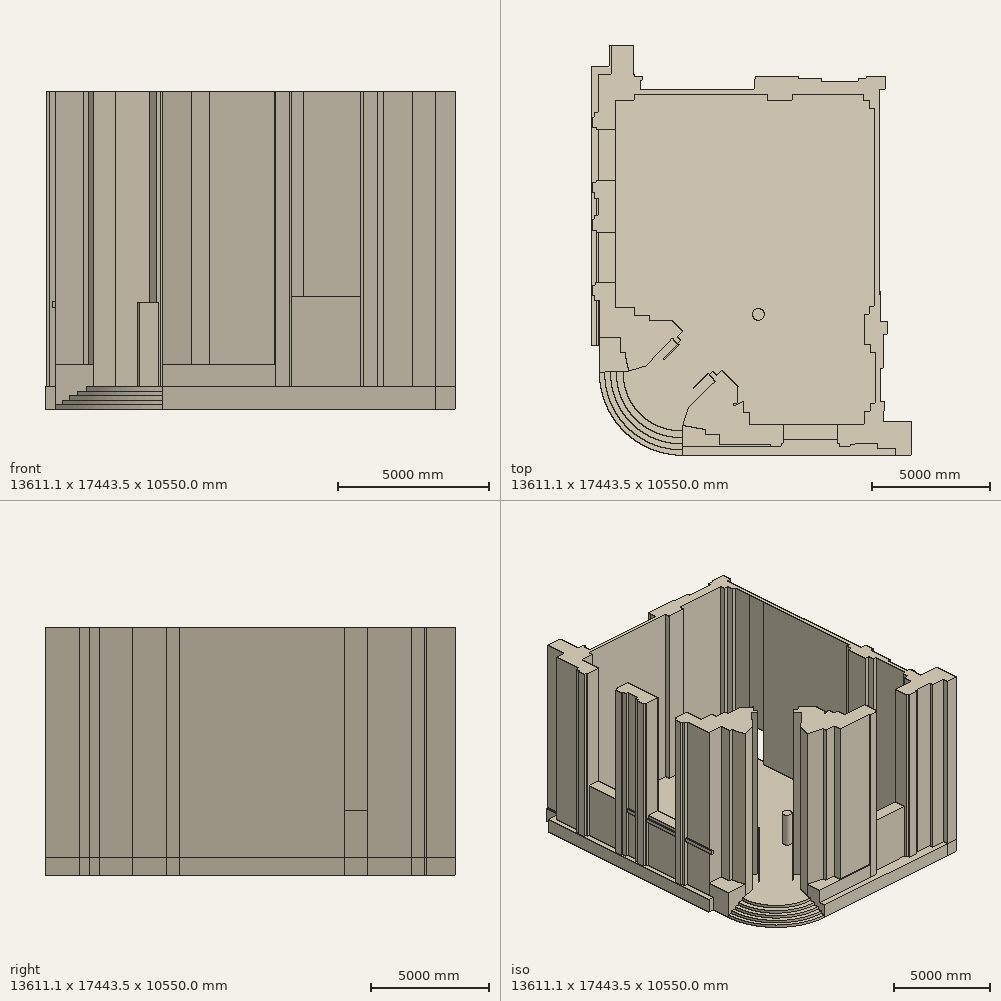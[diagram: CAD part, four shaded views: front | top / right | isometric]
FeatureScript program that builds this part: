
annotation { "Feature Type Name" : "Feature", "Feature Type Description" : "" }
export const myFeature = defineFeature(function(context is Context, id is Id, definition is map)
    precondition{}
    {
        {
            var Q0;
            Q0=qCreatedBy(makeId("Top.planeOp"),FACE);
            var sketch = newSketch(context, id + "F0", { "sketchPlane" : qUnion([Q0])});
            skLineSegment(sketch, "E0", {"start": v(0, 12125) * mm, "end": v(0, 8975) * mm});
            skLineSegment(sketch, "E1", {"start": v(0, 8975) * mm, "end": v(0, 0) * mm});
            skLineSegment(sketch, "E2", {"start": v(0, 0) * mm, "end": v(0, -1070) * mm});
            skLineSegment(sketch, "E3", {"start": v(7940.04, 3339.25) * mm, "end": v(6987.72, 3339.25) * mm});
            skLineSegment(sketch, "E4", {"start": v(6987.72, 3339.25) * mm, "end": v(6987.72, 3558.54) * mm});
            skLineSegment(sketch, "E5", {"start": v(6987.72, 3558.54) * mm, "end": v(6329.76, 3558.54) * mm});
            skLineSegment(sketch, "E6", {"start": v(6329.76, 3558.54) * mm, "end": v(6329.76, 3909.26) * mm});
            skLineSegment(sketch, "E7", {"start": v(6329.76, 3909.26) * mm, "end": v(5538.13, 3909.26) * mm});
            skLineSegment(sketch, "E8", {"start": v(5538.13, 3909.26) * mm, "end": v(5538.13, 4971.17) * mm});
            skLineSegment(sketch, "E9", {"start": v(5538.13, 4971.17) * mm, "end": v(4676.36, 4971.17) * mm});
            skLineSegment(sketch, "E10", {"start": v(4676.36, 4971.17) * mm, "end": v(4676.36, 4850.9) * mm});
            skLineSegment(sketch, "E11", {"start": v(4676.36, 4850.9) * mm, "end": v(4546.1, 4850.9) * mm});
            skLineSegment(sketch, "E12", {"start": v(4546.1, 4850.9) * mm, "end": v(4546.1, 4420.04) * mm});
            skLineSegment(sketch, "E13", {"start": v(4546.1, 4420.04) * mm, "end": v(4676.36, 4420.04) * mm});
            skLineSegment(sketch, "E14", {"start": v(4644.86, 4420.16) * mm, "end": v(4644.86, 4229.77) * mm});
            skLineSegment(sketch, "E15", {"start": v(4644.86, 4229.77) * mm, "end": v(4835.25, 4229.77) * mm});
            skLineSegment(sketch, "E16", {"start": v(4835.25, 4229.77) * mm, "end": v(4835.25, 2626.48) * mm});
            skLineSegment(sketch, "E17", {"start": v(4835.25, 2626.48) * mm, "end": v(5757.14, 2626.48) * mm});
            skLineSegment(sketch, "E18", {"start": v(5757.14, 2626.48) * mm, "end": v(5757.14, 2012.3) * mm});
            skLineSegment(sketch, "E19", {"start": v(5757.14, 2012.3) * mm, "end": v(5947.5, 2012.3) * mm});
            skLineSegment(sketch, "E20", {"start": v(5947.5, 2012.3) * mm, "end": v(6110.95, 1206.17) * mm, "construction": true});
            skLineSegment(sketch, "E21", {"start": v(6110.95, 1206.17) * mm, "end": v(6839.37, 1424) * mm});
            skLineSegment(sketch, "E22", {"start": v(6839.37, 1424) * mm, "end": v(7948.81, 2597.55) * mm});
            skLineSegment(sketch, "E23", {"start": v(7948.81, 2597.55) * mm, "end": v(8010.46, 2533.1) * mm});
            skLineSegment(sketch, "E24", {"start": v(8010.46, 2533.1) * mm, "end": v(8390.4, 2896.52) * mm});
            skLineSegment(sketch, "E25", {"start": v(8390.4, 2896.52) * mm, "end": v(7940.04, 3339.25) * mm});
            skArc(sketch, "E26", {"start": v(5947.5, 2012.3) * mm, "mid": v(5992.6, 1601.8) * mm, "end": v(6110.95, 1206.17) * mm});
            skLineSegment(sketch, "E27", {"start": v(5538.13, 4971.17) * mm, "end": v(5538.13, 7103.34) * mm});
            skLineSegment(sketch, "E28", {"start": v(5538.13, 7103.34) * mm, "end": v(4804.33, 7103.34) * mm});
            skLineSegment(sketch, "E29", {"start": v(4804.33, 7103.34) * mm, "end": v(4804.33, 4971.17) * mm});
            skLineSegment(sketch, "E30", {"start": v(5016.9, 7103.34) * mm, "end": v(5016.9, 4971.17) * mm});
            skLineSegment(sketch, "E31", {"start": v(5171.23, 7103.34) * mm, "end": v(5171.23, 4971.17) * mm});
            skLineSegment(sketch, "E32", {"start": v(5538.13, 7103.34) * mm, "end": v(5538.13, 9326.24) * mm});
            skLineSegment(sketch, "E33", {"start": v(5538.13, 9326.24) * mm, "end": v(4706.43, 9326.24) * mm});
            skLineSegment(sketch, "E34", {"start": v(4706.43, 9326.24) * mm, "end": v(4706.43, 9225.94) * mm});
            skLineSegment(sketch, "E35", {"start": v(4706.43, 9225.94) * mm, "end": v(4546.1, 9225.94) * mm});
            skLineSegment(sketch, "E36", {"start": v(4546.1, 9225.94) * mm, "end": v(4546.1, 8795.12) * mm});
            skLineSegment(sketch, "E37", {"start": v(4546.1, 8795.12) * mm, "end": v(4640.99, 8795.12) * mm});
            skLineSegment(sketch, "E38", {"start": v(4640.99, 8795.12) * mm, "end": v(4640.99, 8570.76) * mm});
            skLineSegment(sketch, "E39", {"start": v(4640.99, 8570.76) * mm, "end": v(4814.59, 8570.76) * mm});
            skLineSegment(sketch, "E40", {"start": v(4814.59, 8570.76) * mm, "end": v(4814.59, 7846.25) * mm});
            skLineSegment(sketch, "E41", {"start": v(4814.59, 7846.25) * mm, "end": v(4639.16, 7846.25) * mm});
            skLineSegment(sketch, "E42", {"start": v(4639.16, 7846.25) * mm, "end": v(4639.16, 7645.84) * mm});
            skLineSegment(sketch, "E43", {"start": v(4639.16, 7645.84) * mm, "end": v(4546.1, 7645.84) * mm});
            skLineSegment(sketch, "E44", {"start": v(4546.1, 7645.84) * mm, "end": v(4546.1, 7191.3) * mm});
            skLineSegment(sketch, "E45", {"start": v(4546.1, 7191.3) * mm, "end": v(4706.43, 7191.3) * mm});
            skLineSegment(sketch, "E46", {"start": v(4706.43, 7191.3) * mm, "end": v(4706.43, 7103.34) * mm});
            skLineSegment(sketch, "E47", {"start": v(4706.43, 7103.34) * mm, "end": v(4804.33, 7103.34) * mm});
            skLineSegment(sketch, "E48", {"start": v(5538.13, 9326.24) * mm, "end": v(5538.13, 11477.09) * mm});
            skLineSegment(sketch, "E49", {"start": v(5538.13, 11477.09) * mm, "end": v(4706.43, 11477.09) * mm});
            skLineSegment(sketch, "E50", {"start": v(5195.88, 11477.09) * mm, "end": v(5195.88, 9326.24) * mm});
            skLineSegment(sketch, "E51", {"start": v(5023.03, 11477.09) * mm, "end": v(5023.03, 9326.24) * mm});
            skLineSegment(sketch, "E52", {"start": v(4822.61, 11477.09) * mm, "end": v(4822.61, 9326.24) * mm});
            skLineSegment(sketch, "E53", {"start": v(5538.13, 11477.09) * mm, "end": v(5538.13, 12718.59) * mm});
            skLineSegment(sketch, "E54", {"start": v(5538.13, 12718.59) * mm, "end": v(6328.59, 12718.59) * mm});
            skLineSegment(sketch, "E55", {"start": v(6328.59, 12718.59) * mm, "end": v(6328.59, 12979.12) * mm});
            skLineSegment(sketch, "E56", {"start": v(6328.59, 12979.12) * mm, "end": v(6579.1, 12979.12) * mm});
            skLineSegment(sketch, "E57", {"start": v(6579.1, 12979.12) * mm, "end": v(6579.1, 13590.38) * mm});
            skLineSegment(sketch, "E58", {"start": v(6579.1, 13590.38) * mm, "end": v(6679.3, 13590.38) * mm});
            skLineSegment(sketch, "E59", {"start": v(6679.3, 13590.38) * mm, "end": v(6679.3, 13743.22) * mm});
            skLineSegment(sketch, "E60", {"start": v(6679.3, 13743.22) * mm, "end": v(6323.82, 13743.22) * mm});
            skLineSegment(sketch, "E61", {"start": v(6323.82, 13743.22) * mm, "end": v(6323.82, 13838.41) * mm});
            skLineSegment(sketch, "E62", {"start": v(6323.82, 13838.41) * mm, "end": v(6296.26, 13838.41) * mm});
            skLineSegment(sketch, "E63", {"start": v(6296.26, 13838.41) * mm, "end": v(6296.26, 15059.07) * mm});
            skLineSegment(sketch, "E64", {"start": v(6296.26, 15059.07) * mm, "end": v(5357.4, 15059.07) * mm});
            skLineSegment(sketch, "E65", {"start": v(5357.4, 15059.07) * mm, "end": v(5357.4, 13838.41) * mm});
            skLineSegment(sketch, "E66", {"start": v(5357.4, 13838.41) * mm, "end": v(4806.28, 13838.41) * mm});
            skLineSegment(sketch, "E67", {"start": v(4806.28, 13838.41) * mm, "end": v(4806.28, 12207.37) * mm});
            skLineSegment(sketch, "E68", {"start": v(4806.28, 12207.37) * mm, "end": v(4616.24, 12207.37) * mm});
            skLineSegment(sketch, "E69", {"start": v(4616.24, 12207.37) * mm, "end": v(4616.24, 12006.96) * mm});
            skLineSegment(sketch, "E70", {"start": v(4616.24, 12006.96) * mm, "end": v(4546.1, 12006.96) * mm});
            skLineSegment(sketch, "E71", {"start": v(4546.1, 12006.96) * mm, "end": v(4546.1, 11556.04) * mm});
            skLineSegment(sketch, "E72", {"start": v(4546.1, 11556.04) * mm, "end": v(4706.43, 11556.04) * mm});
            skLineSegment(sketch, "E73", {"start": v(4706.43, 11556.04) * mm, "end": v(4706.43, 11477.09) * mm});
            skLineSegment(sketch, "E74", {"start": v(4546.1, 11556.04) * mm, "end": v(4546.1, 9225.94) * mm, "construction": true});
            skLineSegment(sketch, "E75", {"start": v(4546.1, 7191.3) * mm, "end": v(4546.1, 4850.9) * mm, "construction": true});
            skLineSegment(sketch, "E76", {"start": v(6579.1, 12979.12) * mm, "end": v(11443.66, 12979.12) * mm});
            skLineSegment(sketch, "E77", {"start": v(11443.66, 12979.12) * mm, "end": v(11443.66, 13185.96) * mm});
            skLineSegment(sketch, "E78", {"start": v(11443.66, 13185.96) * mm, "end": v(6579.1, 13185.96) * mm});
            skLineSegment(sketch, "E79", {"start": v(11443.66, 12979.12) * mm, "end": v(11992.54, 12979.12) * mm});
            skLineSegment(sketch, "E80", {"start": v(11992.54, 12979.12) * mm, "end": v(11992.54, 12727.02) * mm});
            skLineSegment(sketch, "E81", {"start": v(11992.54, 12727.02) * mm, "end": v(13064.75, 12727.02) * mm});
            skLineSegment(sketch, "E82", {"start": v(13064.75, 12727.02) * mm, "end": v(13064.75, 12979.12) * mm});
            skLineSegment(sketch, "E83", {"start": v(13064.75, 12979.12) * mm, "end": v(16070.92, 12979.12) * mm});
            skLineSegment(sketch, "E84", {"start": v(16070.92, 12979.12) * mm, "end": v(16070.92, 12727.02) * mm});
            skLineSegment(sketch, "E85", {"start": v(16070.92, 12727.02) * mm, "end": v(16321.44, 12727.02) * mm});
            skLineSegment(sketch, "E86", {"start": v(16321.44, 12727.02) * mm, "end": v(16321.44, 12366.28) * mm});
            skLineSegment(sketch, "E87", {"start": v(16321.44, 12366.28) * mm, "end": v(16531.87, 12366.28) * mm});
            skLineSegment(sketch, "E88", {"start": v(16531.87, 12366.28) * mm, "end": v(16531.87, 11314.12) * mm});
            skLineSegment(sketch, "E89", {"start": v(16531.87, 11314.12) * mm, "end": v(16752.32, 11314.12) * mm});
            skLineSegment(sketch, "E90", {"start": v(16752.32, 11314.12) * mm, "end": v(16752.32, 13185.96) * mm});
            skLineSegment(sketch, "E91", {"start": v(16752.32, 13185.96) * mm, "end": v(16992.82, 13185.96) * mm});
            skLineSegment(sketch, "E92", {"start": v(16992.82, 13185.96) * mm, "end": v(16992.82, 13739.1) * mm});
            skLineSegment(sketch, "E93", {"start": v(16992.82, 13739.1) * mm, "end": v(16201.19, 13739.1) * mm});
            skLineSegment(sketch, "E94", {"start": v(16201.19, 13739.1) * mm, "end": v(16201.19, 13658.94) * mm});
            skLineSegment(sketch, "E95", {"start": v(16201.19, 13658.94) * mm, "end": v(15860.49, 13658.94) * mm});
            skLineSegment(sketch, "E96", {"start": v(15860.49, 13658.94) * mm, "end": v(15860.49, 13508.63) * mm});
            skLineSegment(sketch, "E97", {"start": v(15860.49, 13508.63) * mm, "end": v(14287.26, 13508.63) * mm});
            skLineSegment(sketch, "E98", {"start": v(14287.26, 13508.63) * mm, "end": v(14287.26, 13658.94) * mm});
            skLineSegment(sketch, "E99", {"start": v(14287.26, 13658.94) * mm, "end": v(13295.22, 13658.94) * mm});
            skLineSegment(sketch, "E100", {"start": v(13295.22, 13658.94) * mm, "end": v(13295.22, 13739.1) * mm});
            skLineSegment(sketch, "E101", {"start": v(13295.22, 13739.1) * mm, "end": v(11495.49, 13739.1) * mm});
            skLineSegment(sketch, "E102", {"start": v(11495.49, 13739.1) * mm, "end": v(11443.66, 13556.66) * mm});
            skLineSegment(sketch, "E103", {"start": v(11443.66, 13556.66) * mm, "end": v(11443.66, 13185.96) * mm});
            skLineSegment(sketch, "E104", {"start": v(16749.46, 10318.63) * mm, "end": v(16529, 10318.63) * mm});
            skLineSegment(sketch, "E105", {"start": v(16529, 10318.63) * mm, "end": v(16529, 3949.74) * mm});
            skLineSegment(sketch, "E106", {"start": v(16529, 3949.74) * mm, "end": v(16348.32, 3949.74) * mm});
            skLineSegment(sketch, "E107", {"start": v(16348.32, 3949.74) * mm, "end": v(16348.32, 3602.54) * mm});
            skLineSegment(sketch, "E108", {"start": v(16348.32, 3602.54) * mm, "end": v(16107.41, 3602.54) * mm});
            skLineSegment(sketch, "E109", {"start": v(16107.41, 3602.54) * mm, "end": v(16107.41, 2348.35) * mm});
            skLineSegment(sketch, "E110", {"start": v(16107.41, 2348.35) * mm, "end": v(16371.6, 2348.35) * mm});
            skLineSegment(sketch, "E111", {"start": v(16371.6, 2348.35) * mm, "end": v(16371.6, 2000.51) * mm});
            skLineSegment(sketch, "E112", {"start": v(16371.6, 2000.51) * mm, "end": v(16571.77, 2000.51) * mm});
            skLineSegment(sketch, "E113", {"start": v(16571.77, 2000.51) * mm, "end": v(16571.77, -172.06) * mm});
            skLineSegment(sketch, "E114", {"start": v(16571.77, -172.06) * mm, "end": v(16387.34, -172.06) * mm});
            skLineSegment(sketch, "E115", {"start": v(16387.34, -172.06) * mm, "end": v(16387.34, -531.4) * mm});
            skLineSegment(sketch, "E116", {"start": v(16387.34, -531.4) * mm, "end": v(16107.41, -531.4) * mm});
            skLineSegment(sketch, "E117", {"start": v(16107.41, -531.4) * mm, "end": v(16107.41, -1052.2) * mm});
            skLineSegment(sketch, "E118", {"start": v(16107.41, -1052.2) * mm, "end": v(14950.76, -1052.2) * mm});
            skLineSegment(sketch, "E119", {"start": v(14950.76, -1052.2) * mm, "end": v(14950.76, -1860.02) * mm});
            skLineSegment(sketch, "E120", {"start": v(14950.76, -1860.02) * mm, "end": v(15058.18, -1860.02) * mm});
            skLineSegment(sketch, "E121", {"start": v(15058.18, -1860.02) * mm, "end": v(15058.18, -1999.96) * mm});
            skLineSegment(sketch, "E122", {"start": v(15058.18, -1999.96) * mm, "end": v(15524.06, -1999.96) * mm});
            skLineSegment(sketch, "E123", {"start": v(15524.06, -1999.96) * mm, "end": v(15524.06, -1918.48) * mm});
            skLineSegment(sketch, "E124", {"start": v(15524.06, -1918.48) * mm, "end": v(15724.23, -1918.48) * mm});
            skLineSegment(sketch, "E125", {"start": v(15724.23, -1918.48) * mm, "end": v(15724.23, -1883.05) * mm});
            skLineSegment(sketch, "E126", {"start": v(15724.23, -1883.05) * mm, "end": v(16678.15, -1883.05) * mm});
            skLineSegment(sketch, "E127", {"start": v(16678.15, -1883.05) * mm, "end": v(16678.15, -2084.88) * mm});
            skLineSegment(sketch, "E128", {"start": v(16678.15, -2084.88) * mm, "end": v(17458.3, -2084.88) * mm});
            skLineSegment(sketch, "E129", {"start": v(17458.3, -2084.88) * mm, "end": v(17458.3, -2384.45) * mm});
            skLineSegment(sketch, "E130", {"start": v(17458.3, -2384.45) * mm, "end": v(18116.83, -2384.45) * mm});
            skLineSegment(sketch, "E131", {"start": v(18116.83, -2384.45) * mm, "end": v(18116.83, -946.5) * mm});
            skLineSegment(sketch, "E132", {"start": v(18116.83, -946.5) * mm, "end": v(16924.38, -946.5) * mm});
            skLineSegment(sketch, "E133", {"start": v(16924.38, -946.5) * mm, "end": v(16924.38, -515.61) * mm});
            skLineSegment(sketch, "E134", {"start": v(16924.38, -515.61) * mm, "end": v(16984.5, -515.61) * mm});
            skLineSegment(sketch, "E135", {"start": v(16984.5, -515.61) * mm, "end": v(16984.5, -104.77) * mm});
            skLineSegment(sketch, "E136", {"start": v(16984.5, -104.77) * mm, "end": v(16784.1, -104.77) * mm});
            skLineSegment(sketch, "E137", {"start": v(16784.1, -104.77) * mm, "end": v(16784.1, 1320.73) * mm});
            skLineSegment(sketch, "E138", {"start": v(16784.1, 1320.73) * mm, "end": v(16914.18, 1320.73) * mm});
            skLineSegment(sketch, "E139", {"start": v(16914.18, 1320.73) * mm, "end": v(16914.18, 2753.98) * mm});
            skLineSegment(sketch, "E140", {"start": v(16914.18, 2753.98) * mm, "end": v(17110.48, 2753.98) * mm});
            skLineSegment(sketch, "E141", {"start": v(17110.48, 2753.98) * mm, "end": v(17110.48, 3310.12) * mm});
            skLineSegment(sketch, "E142", {"start": v(17110.48, 3310.12) * mm, "end": v(16784.1, 3310.12) * mm});
            skLineSegment(sketch, "E143", {"start": v(16784.1, 3310.12) * mm, "end": v(16749.46, 10318.63) * mm});
            skLineSegment(sketch, "E144", {"start": v(10955.86, -104.77) * mm, "end": v(10957.98, -534) * mm});
            skLineSegment(sketch, "E145", {"start": v(10957.98, -534) * mm, "end": v(11210.94, -534) * mm});
            skLineSegment(sketch, "E146", {"start": v(11210.94, -534) * mm, "end": v(11213.5, -1052.2) * mm});
            skLineSegment(sketch, "E147", {"start": v(11213.5, -1052.2) * mm, "end": v(12670.58, -1052.2) * mm});
            skLineSegment(sketch, "E148", {"start": v(12670.58, -1052.2) * mm, "end": v(12674.57, -1860.02) * mm});
            skLineSegment(sketch, "E149", {"start": v(12674.57, -1860.02) * mm, "end": v(12599.73, -1860.02) * mm});
            skLineSegment(sketch, "E150", {"start": v(12599.73, -1860.02) * mm, "end": v(12600.5, -2014.87) * mm});
            skLineSegment(sketch, "E151", {"start": v(12600.5, -2014.87) * mm, "end": v(12124.99, -2014.87) * mm});
            skLineSegment(sketch, "E152", {"start": v(12124.99, -2014.87) * mm, "end": v(12124.6, -1937.04) * mm});
            skLineSegment(sketch, "E153", {"start": v(12124.6, -1937.04) * mm, "end": v(9963.87, -1937.04) * mm});
            skLineSegment(sketch, "E154", {"start": v(9963.87, -1937.04) * mm, "end": v(9961.67, -1490.58) * mm});
            skLineSegment(sketch, "E155", {"start": v(9961.67, -1490.58) * mm, "end": v(9368.68, -1490.58) * mm});
            skLineSegment(sketch, "E156", {"start": v(9368.68, -1490.58) * mm, "end": v(9367.67, -1285.06) * mm});
            skLineSegment(sketch, "E157", {"start": v(9367.67, -1285.06) * mm, "end": v(8390.86, -1107.98) * mm});
            skLineSegment(sketch, "E158", {"start": v(8390.86, -1107.98) * mm, "end": v(8624.7, -378.16) * mm});
            skLineSegment(sketch, "E159", {"start": v(8624.7, -378.16) * mm, "end": v(9779.65, 762.62) * mm});
            skLineSegment(sketch, "E160", {"start": v(9779.65, 762.62) * mm, "end": v(9691.6, 851.76) * mm});
            skLineSegment(sketch, "E161", {"start": v(9691.6, 851.76) * mm, "end": v(10076.1, 1231.53) * mm});
            skLineSegment(sketch, "E162", {"start": v(10076.1, 1231.53) * mm, "end": v(10739.2, 560.18) * mm});
            skLineSegment(sketch, "E163", {"start": v(10739.2, 560.18) * mm, "end": v(10707.47, -183.95) * mm});
            skLineSegment(sketch, "E164", {"start": v(10707.47, -183.95) * mm, "end": v(10517.08, -183.95) * mm});
            skLineSegment(sketch, "E165", {"start": v(10517.08, -183.95) * mm, "end": v(10588.48, -271.63) * mm});
            skLineSegment(sketch, "E166", {"start": v(10588.48, -271.63) * mm, "end": v(10955.86, -104.77) * mm});
            skLineSegment(sketch, "E167", {"start": v(9691.6, 851.76) * mm, "end": v(9504.05, 1041.64) * mm});
            skPoint(sketch, "E167.endSnap0", {"position": v(9883.85, 1041.64) * mm});
            skLineSegment(sketch, "E168", {"start": v(9504.05, 1041.64) * mm, "end": v(9660, 1195.68) * mm});
            skLineSegment(sketch, "E169", {"start": v(9660, 1195.68) * mm, "end": v(9847.55, 1005.8) * mm});
            skLineSegment(sketch, "E170", {"start": v(9489.72, 1069.4) * mm, "end": v(8853.27, 440.76) * mm});
            skLineSegment(sketch, "E171", {"start": v(8853.27, 440.76) * mm, "end": v(8828.52, 465.82) * mm});
            skLineSegment(sketch, "E172", {"start": v(8828.52, 465.82) * mm, "end": v(9464.77, 1094.27) * mm});
            skLineSegment(sketch, "E173", {"start": v(9464.77, 1094.27) * mm, "end": v(9489.72, 1069.4) * mm});
            skLineSegment(sketch, "E174", {"start": v(8155.17, 2671.52) * mm, "end": v(8318.08, 2501.2) * mm});
            skLineSegment(sketch, "E175", {"start": v(8318.08, 2501.2) * mm, "end": v(8175.6, 2360.46) * mm});
            skLineSegment(sketch, "E176", {"start": v(8175.6, 2360.46) * mm, "end": v(8010.46, 2533.1) * mm});
            skLineSegment(sketch, "E177", {"start": v(8208.1, 2343.48) * mm, "end": v(7569.28, 1709.68) * mm});
            skLineSegment(sketch, "E178", {"start": v(7569.28, 1709.68) * mm, "end": v(7610.45, 1668.18) * mm});
            skLineSegment(sketch, "E179", {"start": v(7610.45, 1668.18) * mm, "end": v(8251.91, 2304.62) * mm});
            skLineSegment(sketch, "E180", {"start": v(8251.91, 2304.62) * mm, "end": v(8208.1, 2343.48) * mm});
            skLineSegment(sketch, "E181", {"start": v(14950.76, -1052.2) * mm, "end": v(12670.58, -1052.2) * mm});
            skLineSegment(sketch, "E182", {"start": v(12672.08, -1355.72) * mm, "end": v(14950.76, -1344.46) * mm});
            skLineSegment(sketch, "E183", {"start": v(14950.76, -1511.59) * mm, "end": v(12672.85, -1511.59) * mm});
            skLineSegment(sketch, "E184", {"start": v(12673.9, -1724.2) * mm, "end": v(14950.76, -1712.95) * mm});
            skArc(sketch, "E185", {"start": v(6839.37, 1424) * mm, "mid": v(7508.6, 301.59) * mm, "end": v(8624.7, -378.16) * mm});
            skLineSegment(sketch, "E186", {"start": v(4835.25, 2626.48) * mm, "end": v(4835.25, 1157.72) * mm});
            skLineSegment(sketch, "E187", {"start": v(4835.25, 1157.72) * mm, "end": v(6110.95, 1206.17) * mm});
            skLineSegment(sketch, "E188", {"start": v(8390.86, -1107.98) * mm, "end": v(8390.86, -2375.98) * mm});
            skLineSegment(sketch, "E189", {"start": v(8390.86, -2375.98) * mm, "end": v(17458.3, -2384.45) * mm});
            skArc(sketch, "E190", {"start": v(5855.53, 1196.47) * mm, "mid": v(6569.5, -622.26) * mm, "end": v(8390.86, -1329.48) * mm});
            skArc(sketch, "E191", {"start": v(5563.67, 1185.38) * mm, "mid": v(6369.39, -830.3) * mm, "end": v(8390.86, -1621.35) * mm});
            skArc(sketch, "E192", {"start": v(5314.58, 1175.92) * mm, "mid": v(6199.93, -1011.75) * mm, "end": v(8390.86, -1889) * mm});
            skArc(sketch, "E193", {"start": v(5065.76, 1166.47) * mm, "mid": v(6026.82, -1192.56) * mm, "end": v(8390.86, -2141.24) * mm});
            skArc(sketch, "E194", {"start": v(4835.25, 1157.72) * mm, "mid": v(5878, -1348.75) * mm, "end": v(8390.86, -2375.98) * mm});
            skLineSegment(sketch, "E195", {"start": v(16749.46, 10318.63) * mm, "end": v(16752.32, 11314.12) * mm});
            skLineSegment(sketch, "E196", {"start": v(16531.87, 11314.12) * mm, "end": v(16529, 10318.63) * mm});
            skLineSegment(sketch, "E197", {"start": v(12124.99, -2014.87) * mm, "end": v(8390.86, -2011.38) * mm});
            skLineSegment(sketch, "E198", {"start": v(4835.25, 2295.94) * mm, "end": v(4505.74, 2295.94) * mm});
            skLineSegment(sketch, "E199", {"start": v(4505.74, 2295.94) * mm, "end": v(4505.74, 14151.04) * mm});
            skLineSegment(sketch, "E200", {"start": v(4505.74, 14151.04) * mm, "end": v(5251.5, 14151.04) * mm});
            skLineSegment(sketch, "E201", {"start": v(5251.5, 14151.04) * mm, "end": v(5251.5, 15059.07) * mm});
            skLineSegment(sketch, "E202", {"start": v(5251.5, 15059.07) * mm, "end": v(5357.4, 15059.07) * mm});
            skSolve(sketch);
        }
        {
            var Q0;
            Q0=makeQuery(id+"F0.imprint","IMPRINT",FACE,{"disambiguationData":[TD([[makeQuery(id+"F0.imprint","IMPRINT",EDGE,{"derivedFrom":sQuery(id+"F0.wireOp",EDGE,"E3")}),1.0]])]});
            var Q1;
            {var subQ5=sQuery(id+"F0.wireOp",EDGE,"E32");Q1=makeQuery(id+"F0.imprint","IMPRINT",FACE,{"disambiguationData":[TD([[makeQuery(id+"F0.imprint","IMPRINT",EDGE,{"derivedFrom":subQ5}),1.0]])]});}
            var Q2;
            {var subQ8=sQuery(id+"F0.wireOp",EDGE,"E53");Q2=makeQuery(id+"F0.imprint","IMPRINT",FACE,{"disambiguationData":[TD([[makeQuery(id+"F0.imprint","IMPRINT",EDGE,{"derivedFrom":subQ8}),1.0]])]});}
            var Q3;
            {var subQ0=sQuery(id+"F0.wireOp",EDGE,"E76");Q3=makeQuery(id+"F0.imprint","IMPRINT",FACE,{"disambiguationData":[TD([[makeQuery(id+"F0.imprint","IMPRINT",EDGE,{"derivedFrom":subQ0}),1.0]])]});}
            var Q4;
            Q4=makeQuery(id+"F0.imprint","IMPRINT",FACE,{"disambiguationData":[TD([[makeQuery(id+"F0.imprint","IMPRINT",EDGE,{"derivedFrom":sQuery(id+"F0.wireOp",EDGE,"E77")}),-1.0]])]});
            var Q5;
            Q5=makeQuery(id+"F0.imprint","IMPRINT",FACE,{"disambiguationData":[TD([[makeQuery(id+"F0.imprint","IMPRINT",EDGE,{"derivedFrom":sQuery(id+"F0.wireOp",EDGE,"E104")}),1.0]])]});
            var Q6;
            Q6=makeQuery(id+"F0.imprint","IMPRINT",FACE,{"disambiguationData":[TD([[makeQuery(id+"F0.imprint","IMPRINT",EDGE,{"derivedFrom":sQuery(id+"F0.wireOp",EDGE,"E144")}),-1.0]])]});
            var Q7;
            {var subQ0=sQuery(id+"F0.wireOp",EDGE,"E167");Q7=makeQuery(id+"F0.imprint","IMPRINT",FACE,{"disambiguationData":[TD([[makeQuery(id+"F0.imprint","IMPRINT",EDGE,{"derivedFrom":subQ0}),-1.0]])]});}
            var Q8;
            {var subQ2=sQuery(id+"F0.wireOp",EDGE,"E174");Q8=makeQuery(id+"F0.imprint","IMPRINT",FACE,{"disambiguationData":[TD([[makeQuery(id+"F0.imprint","IMPRINT",EDGE,{"derivedFrom":subQ2}),-1.0]])]});}
            extrude(context, id + "F1", {"entities" : qUnion([Q0, Q1, Q2, Q3, Q4, Q5, Q6, Q7, Q8]), "depth" : 9800 * mm, "offsetDistance" : 25 * mm});
        }
        {
            var Q0;
            Q0=makeQuery(id+"F0.imprint","IMPRINT",FACE,{"disambiguationData":[TD([[makeQuery(id+"F0.imprint","IMPRINT",EDGE,{"derivedFrom":sQuery(id+"F0.wireOp",EDGE,"E89")}),-1.0]])]});
            var Q1;
            Q1=makeQuery(id+"F1.opExtrude","CAP_FACE",FACE,{"disambiguationData":[OSD([sQuery(id+"F0.wireOp",EDGE,"E49"),sQuery(id+"F0.wireOp",EDGE,"E53"),sQuery(id+"F0.wireOp",EDGE,"E54"),sQuery(id+"F0.wireOp",EDGE,"E55"),sQuery(id+"F0.wireOp",EDGE,"E56"),sQuery(id+"F0.wireOp",EDGE,"E57"),sQuery(id+"F0.wireOp",EDGE,"E58"),sQuery(id+"F0.wireOp",EDGE,"E59"),sQuery(id+"F0.wireOp",EDGE,"E60"),sQuery(id+"F0.wireOp",EDGE,"E61"),sQuery(id+"F0.wireOp",EDGE,"E62"),sQuery(id+"F0.wireOp",EDGE,"E63"),sQuery(id+"F0.wireOp",EDGE,"E64"),sQuery(id+"F0.wireOp",EDGE,"E65"),sQuery(id+"F0.wireOp",EDGE,"E66"),sQuery(id+"F0.wireOp",EDGE,"E67"),sQuery(id+"F0.wireOp",EDGE,"E68"),sQuery(id+"F0.wireOp",EDGE,"E69"),sQuery(id+"F0.wireOp",EDGE,"E70"),sQuery(id+"F0.wireOp",EDGE,"E71"),sQuery(id+"F0.wireOp",EDGE,"E72"),sQuery(id+"F0.wireOp",EDGE,"E73"),sQuery(id+"F0.wireOp",EDGE,"E76"),sQuery(id+"F0.wireOp",EDGE,"E78"),sQuery(id+"F0.wireOp",EDGE,"E79"),sQuery(id+"F0.wireOp",EDGE,"E80"),sQuery(id+"F0.wireOp",EDGE,"E81"),sQuery(id+"F0.wireOp",EDGE,"E82"),sQuery(id+"F0.wireOp",EDGE,"E83"),sQuery(id+"F0.wireOp",EDGE,"E84"),sQuery(id+"F0.wireOp",EDGE,"E85"),sQuery(id+"F0.wireOp",EDGE,"E86"),sQuery(id+"F0.wireOp",EDGE,"E87"),sQuery(id+"F0.wireOp",EDGE,"E88"),sQuery(id+"F0.wireOp",EDGE,"E89"),sQuery(id+"F0.wireOp",EDGE,"E90"),sQuery(id+"F0.wireOp",EDGE,"E91"),sQuery(id+"F0.wireOp",EDGE,"E92"),sQuery(id+"F0.wireOp",EDGE,"E93"),sQuery(id+"F0.wireOp",EDGE,"E94"),sQuery(id+"F0.wireOp",EDGE,"E95"),sQuery(id+"F0.wireOp",EDGE,"E96"),sQuery(id+"F0.wireOp",EDGE,"E97"),sQuery(id+"F0.wireOp",EDGE,"E98"),sQuery(id+"F0.wireOp",EDGE,"E99"),sQuery(id+"F0.wireOp",EDGE,"E100"),sQuery(id+"F0.wireOp",EDGE,"E101"),sQuery(id+"F0.wireOp",EDGE,"E102"),sQuery(id+"F0.wireOp",EDGE,"E103")])],"isStart":false});
            extrude(context, id + "F2", {"entities" : qUnion([Q0]), "operationType" : NewBodyOperationType.ADD, "endBound" : BoundingType.UP_TO_SURFACE, "depth" : 15900 * mm, "endBoundEntityFace" : qUnion([Q1]), "offsetDistance" : 25 * mm, "hasSecondDirection" : true, "secondDirectionOppositeDirection" : false, "secondDirectionDepth" : 2000 * mm});
        }
        {
            var Q0;
            {var subQ6=sQuery(id+"F0.wireOp",EDGE,"E17");Q0=makeQuery(id+"F0.imprint","IMPRINT",FACE,{"disambiguationData":[TD([[makeQuery(id+"F0.imprint","IMPRINT",EDGE,{"derivedFrom":subQ6}),-1.0]])]});}
            var Q1;
            Q1=makeQuery(id+"F0.imprint","IMPRINT",FACE,{"disambiguationData":[TD([[makeQuery(id+"F0.imprint","IMPRINT",EDGE,{"derivedFrom":sQuery(id+"F0.wireOp",EDGE,"E152")}),1.0]])]});
            extrude(context, id + "F3", {"entities" : qUnion([Q0, Q1]), "depth" : 730 * mm, "offsetDistance" : 25 * mm, "hasSecondDirection" : true, "secondDirectionOppositeDirection" : true, "secondDirectionDepth" : 750 * mm});
        }
        {
            var Q0;
            Q0=makeQuery(id+"F0.imprint","IMPRINT",FACE,{"disambiguationData":[TD([[makeQuery(id+"F0.imprint","IMPRINT",EDGE,{"derivedFrom":sQuery(id+"F0.wireOp",EDGE,"E170")}),-1.0]])]});
            var Q1;
            Q1=makeQuery(id+"F0.imprint","IMPRINT",FACE,{"disambiguationData":[TD([[makeQuery(id+"F0.imprint","IMPRINT",EDGE,{"derivedFrom":sQuery(id+"F0.wireOp",EDGE,"E177")}),1.0]])]});
            extrude(context, id + "F4", {"entities" : qUnion([Q0, Q1]), "depth" : 2800 * mm, "offsetDistance" : 25 * mm});
        }
        {
            var Q0;
            Q0=makeQuery(id+"F0.imprint","IMPRINT",FACE,{"disambiguationData":[TD([[makeQuery(id+"F0.imprint","IMPRINT",EDGE,{"derivedFrom":sQuery(id+"F0.wireOp",EDGE,"E3")}),-1.0]])]});
            var Q1;
            Q1=makeQuery(id+"F0.imprint","IMPRINT",FACE,{"disambiguationData":[TD([[makeQuery(id+"F0.imprint","IMPRINT",EDGE,{"derivedFrom":sQuery(id+"F0.wireOp",EDGE,"E177")}),1.0]])]});
            var Q2;
            {var subQ2=sQuery(id+"F0.wireOp",EDGE,"E174");Q2=makeQuery(id+"F0.imprint","IMPRINT",FACE,{"disambiguationData":[TD([[makeQuery(id+"F0.imprint","IMPRINT",EDGE,{"derivedFrom":subQ2}),-1.0]])]});}
            var Q3;
            Q3=makeQuery(id+"F0.imprint","IMPRINT",FACE,{"disambiguationData":[TD([[makeQuery(id+"F0.imprint","IMPRINT",EDGE,{"derivedFrom":sQuery(id+"F0.wireOp",EDGE,"E3")}),1.0]])]});
            var Q4;
            Q4=makeQuery(id+"F0.imprint","IMPRINT",FACE,{"disambiguationData":[TD([[makeQuery(id+"F0.imprint","IMPRINT",EDGE,{"derivedFrom":sQuery(id+"F0.wireOp",EDGE,"E144")}),-1.0]])]});
            var Q5;
            {var subQ0=sQuery(id+"F0.wireOp",EDGE,"E27");Q5=makeQuery(id+"F0.imprint","IMPRINT",FACE,{"disambiguationData":[TD([[makeQuery(id+"F0.imprint","IMPRINT",EDGE,{"derivedFrom":subQ0}),1.0]])]});}
            var Q6;
            {var subQ0=sQuery(id+"F0.wireOp",EDGE,"E30");Q6=makeQuery(id+"F0.imprint","IMPRINT",FACE,{"disambiguationData":[TD([[makeQuery(id+"F0.imprint","IMPRINT",EDGE,{"derivedFrom":subQ0}),1.0]])]});}
            var Q7;
            {var subQ0=sQuery(id+"F0.wireOp",EDGE,"E29");Q7=makeQuery(id+"F0.imprint","IMPRINT",FACE,{"disambiguationData":[TD([[makeQuery(id+"F0.imprint","IMPRINT",EDGE,{"derivedFrom":subQ0}),1.0]])]});}
            var Q8;
            {var subQ5=sQuery(id+"F0.wireOp",EDGE,"E32");Q8=makeQuery(id+"F0.imprint","IMPRINT",FACE,{"disambiguationData":[TD([[makeQuery(id+"F0.imprint","IMPRINT",EDGE,{"derivedFrom":subQ5}),1.0]])]});}
            var Q9;
            {var subQ0=sQuery(id+"F0.wireOp",EDGE,"E48");Q9=makeQuery(id+"F0.imprint","IMPRINT",FACE,{"disambiguationData":[TD([[makeQuery(id+"F0.imprint","IMPRINT",EDGE,{"derivedFrom":subQ0}),1.0]])]});}
            var Q10;
            {var subQ0=sQuery(id+"F0.wireOp",EDGE,"E50");Q10=makeQuery(id+"F0.imprint","IMPRINT",FACE,{"disambiguationData":[TD([[makeQuery(id+"F0.imprint","IMPRINT",EDGE,{"derivedFrom":subQ0}),-1.0]])]});}
            var Q11;
            {var subQ0=sQuery(id+"F0.wireOp",EDGE,"E51");Q11=makeQuery(id+"F0.imprint","IMPRINT",FACE,{"disambiguationData":[TD([[makeQuery(id+"F0.imprint","IMPRINT",EDGE,{"derivedFrom":subQ0}),-1.0]])]});}
            var Q12;
            {var subQ4=sQuery(id+"F0.wireOp",EDGE,"E10");Q12=makeQuery(id+"F0.imprint","IMPRINT",FACE,{"disambiguationData":[TD([[makeQuery(id+"F0.imprint","IMPRINT",EDGE,{"derivedFrom":subQ4}),-1.0]])]});}
            var Q13;
            {var subQ1=sQuery(id+"F0.wireOp",EDGE,"E21");Q13=makeQuery(id+"F0.imprint","IMPRINT",FACE,{"disambiguationData":[TD([[makeQuery(id+"F0.imprint","IMPRINT",EDGE,{"derivedFrom":subQ1}),-1.0]])]});}
            var Q14;
            {var subQ0=sQuery(id+"F0.wireOp",EDGE,"E181");Q14=makeQuery(id+"F0.imprint","IMPRINT",FACE,{"disambiguationData":[TD([[makeQuery(id+"F0.imprint","IMPRINT",EDGE,{"derivedFrom":subQ0}),1.0]])]});}
            var Q15;
            {var subQ0=sQuery(id+"F0.wireOp",EDGE,"E182");Q15=makeQuery(id+"F0.imprint","IMPRINT",FACE,{"disambiguationData":[TD([[makeQuery(id+"F0.imprint","IMPRINT",EDGE,{"derivedFrom":subQ0}),-1.0]])]});}
            var Q16;
            {var subQ0=sQuery(id+"F0.wireOp",EDGE,"E183");Q16=makeQuery(id+"F0.imprint","IMPRINT",FACE,{"disambiguationData":[TD([[makeQuery(id+"F0.imprint","IMPRINT",EDGE,{"derivedFrom":subQ0}),1.0]])]});}
            var Q17;
            {var subQ3=sQuery(id+"F0.wireOp",EDGE,"E120");Q17=makeQuery(id+"F0.imprint","IMPRINT",FACE,{"disambiguationData":[TD([[makeQuery(id+"F0.imprint","IMPRINT",EDGE,{"derivedFrom":subQ3}),-1.0]])]});}
            var Q18;
            Q18=makeQuery(id+"F0.imprint","IMPRINT",FACE,{"disambiguationData":[TD([[makeQuery(id+"F0.imprint","IMPRINT",EDGE,{"derivedFrom":sQuery(id+"F0.wireOp",EDGE,"E104")}),1.0]])]});
            var Q19;
            Q19=makeQuery(id+"F0.imprint","IMPRINT",FACE,{"disambiguationData":[TD([[makeQuery(id+"F0.imprint","IMPRINT",EDGE,{"derivedFrom":sQuery(id+"F0.wireOp",EDGE,"E89")}),-1.0]])]});
            var Q20;
            Q20=makeQuery(id+"F0.imprint","IMPRINT",FACE,{"disambiguationData":[TD([[makeQuery(id+"F0.imprint","IMPRINT",EDGE,{"derivedFrom":sQuery(id+"F0.wireOp",EDGE,"E77")}),-1.0]])]});
            var Q21;
            {var subQ0=sQuery(id+"F0.wireOp",EDGE,"E76");Q21=makeQuery(id+"F0.imprint","IMPRINT",FACE,{"disambiguationData":[TD([[makeQuery(id+"F0.imprint","IMPRINT",EDGE,{"derivedFrom":subQ0}),1.0]])]});}
            var Q22;
            {var subQ8=sQuery(id+"F0.wireOp",EDGE,"E53");Q22=makeQuery(id+"F0.imprint","IMPRINT",FACE,{"disambiguationData":[TD([[makeQuery(id+"F0.imprint","IMPRINT",EDGE,{"derivedFrom":subQ8}),1.0]])]});}
            var Q23;
            {var subQ0=sQuery(id+"F0.wireOp",EDGE,"E167");Q23=makeQuery(id+"F0.imprint","IMPRINT",FACE,{"disambiguationData":[TD([[makeQuery(id+"F0.imprint","IMPRINT",EDGE,{"derivedFrom":subQ0}),-1.0]])]});}
            var Q24;
            Q24=makeQuery(id+"F0.imprint","IMPRINT",FACE,{"disambiguationData":[TD([[makeQuery(id+"F0.imprint","IMPRINT",EDGE,{"derivedFrom":sQuery(id+"F0.wireOp",EDGE,"E170")}),-1.0]])]});
            var Q25;
            Q25=makeQuery(id+"F3.opExtrude","CAP_FACE",FACE,{"disambiguationData":[OSD([sQuery(id+"F0.wireOp",EDGE,"E17"),sQuery(id+"F0.wireOp",EDGE,"E18"),sQuery(id+"F0.wireOp",EDGE,"E19"),sQuery(id+"F0.wireOp",EDGE,"E26"),sQuery(id+"F0.wireOp",EDGE,"E186"),sQuery(id+"F0.wireOp",EDGE,"E187")])],"isStart":true});
            extrude(context, id + "F5", {"entities" : qUnion([Q0, Q1, Q2, Q3, Q4, Q5, Q6, Q7, Q8, Q9, Q10, Q11, Q12, Q13, Q14, Q15, Q16, Q17, Q18, Q19, Q20, Q21, Q22, Q23, Q24]), "endBound" : BoundingType.UP_TO_SURFACE, "oppositeDirection" : true, "depth" : 600 * mm, "endBoundEntityFace" : qUnion([Q25]), "offsetDistance" : 25 * mm});
        }
        {
            var Q0;
            {var subQ0=sQuery(id+"F0.wireOp",EDGE,"E190");Q0=makeQuery(id+"F0.imprint","IMPRINT",FACE,{"disambiguationData":[TD([[makeQuery(id+"F0.imprint","IMPRINT",EDGE,{"derivedFrom":subQ0}),-1.0]])]});}
            var Q1;
            Q1=makeQuery(id+"F3.opExtrude","CAP_FACE",FACE,{"disambiguationData":[OSD([sQuery(id+"F0.wireOp",EDGE,"E17"),sQuery(id+"F0.wireOp",EDGE,"E18"),sQuery(id+"F0.wireOp",EDGE,"E19"),sQuery(id+"F0.wireOp",EDGE,"E26"),sQuery(id+"F0.wireOp",EDGE,"E186"),sQuery(id+"F0.wireOp",EDGE,"E187")])],"isStart":true});
            extrude(context, id + "F6", {"entities" : qUnion([Q0]), "operationType" : NewBodyOperationType.ADD, "endBound" : BoundingType.UP_TO_SURFACE, "oppositeDirection" : true, "depth" : 110 * mm, "endBoundEntityFace" : qUnion([Q1]), "offsetDistance" : 25 * mm, "hasSecondDirection" : true, "secondDirectionOppositeDirection" : true, "secondDirectionDepth" : 150 * mm});
        }
        {
            var Q0;
            {var subQ0=sQuery(id+"F0.wireOp",EDGE,"E191");Q0=makeQuery(id+"F0.imprint","IMPRINT",FACE,{"disambiguationData":[TD([[makeQuery(id+"F0.imprint","IMPRINT",EDGE,{"derivedFrom":subQ0}),-1.0]])]});}
            var Q1;
            Q1=makeQuery(id+"F3.opExtrude","CAP_FACE",FACE,{"disambiguationData":[OSD([sQuery(id+"F0.wireOp",EDGE,"E17"),sQuery(id+"F0.wireOp",EDGE,"E18"),sQuery(id+"F0.wireOp",EDGE,"E19"),sQuery(id+"F0.wireOp",EDGE,"E26"),sQuery(id+"F0.wireOp",EDGE,"E186"),sQuery(id+"F0.wireOp",EDGE,"E187")])],"isStart":true});
            extrude(context, id + "F7", {"entities" : qUnion([Q0]), "operationType" : NewBodyOperationType.ADD, "endBound" : BoundingType.UP_TO_SURFACE, "oppositeDirection" : true, "depth" : 25 * mm, "endBoundEntityFace" : qUnion([Q1]), "offsetDistance" : 25 * mm, "hasSecondDirection" : true, "secondDirectionOppositeDirection" : true, "secondDirectionDepth" : 300 * mm});
        }
        {
            var Q0;
            {var subQ0=sQuery(id+"F0.wireOp",EDGE,"E192");Q0=makeQuery(id+"F0.imprint","IMPRINT",FACE,{"disambiguationData":[TD([[makeQuery(id+"F0.imprint","IMPRINT",EDGE,{"derivedFrom":subQ0}),-1.0]])]});}
            var Q1;
            Q1=makeQuery(id+"F3.opExtrude","CAP_FACE",FACE,{"disambiguationData":[OSD([sQuery(id+"F0.wireOp",EDGE,"E17"),sQuery(id+"F0.wireOp",EDGE,"E18"),sQuery(id+"F0.wireOp",EDGE,"E19"),sQuery(id+"F0.wireOp",EDGE,"E26"),sQuery(id+"F0.wireOp",EDGE,"E186"),sQuery(id+"F0.wireOp",EDGE,"E187")])],"isStart":true});
            extrude(context, id + "F8", {"entities" : qUnion([Q0]), "operationType" : NewBodyOperationType.ADD, "endBound" : BoundingType.UP_TO_SURFACE, "oppositeDirection" : true, "depth" : 25 * mm, "endBoundEntityFace" : qUnion([Q1]), "offsetDistance" : 25 * mm, "hasSecondDirection" : true, "secondDirectionOppositeDirection" : true, "secondDirectionDepth" : 450 * mm});
        }
        {
            var Q0;
            {var subQ2=sQuery(id+"F0.wireOp",EDGE,"E193");Q0=makeQuery(id+"F0.imprint","IMPRINT",FACE,{"disambiguationData":[TD([[makeQuery(id+"F0.imprint","IMPRINT",EDGE,{"derivedFrom":subQ2}),-1.0]])]});}
            var Q1;
            Q1=makeQuery(id+"F3.opExtrude","CAP_FACE",FACE,{"disambiguationData":[OSD([sQuery(id+"F0.wireOp",EDGE,"E17"),sQuery(id+"F0.wireOp",EDGE,"E18"),sQuery(id+"F0.wireOp",EDGE,"E19"),sQuery(id+"F0.wireOp",EDGE,"E26"),sQuery(id+"F0.wireOp",EDGE,"E186"),sQuery(id+"F0.wireOp",EDGE,"E187")])],"isStart":true});
            extrude(context, id + "F9", {"entities" : qUnion([Q0]), "operationType" : NewBodyOperationType.ADD, "endBound" : BoundingType.UP_TO_SURFACE, "oppositeDirection" : true, "depth" : 25 * mm, "endBoundEntityFace" : qUnion([Q1]), "offsetDistance" : 25 * mm, "hasSecondDirection" : true, "secondDirectionOppositeDirection" : true, "secondDirectionDepth" : 600 * mm});
        }
        {
            var Q0;
            {var subQ0=sQuery(id+"F0.wireOp",EDGE,"E181");Q0=makeQuery(id+"F0.imprint","IMPRINT",FACE,{"disambiguationData":[TD([[makeQuery(id+"F0.imprint","IMPRINT",EDGE,{"derivedFrom":subQ0}),1.0]])]});}
            var Q1;
            {var subQ0=sQuery(id+"F0.wireOp",EDGE,"E182");Q1=makeQuery(id+"F0.imprint","IMPRINT",FACE,{"disambiguationData":[TD([[makeQuery(id+"F0.imprint","IMPRINT",EDGE,{"derivedFrom":subQ0}),-1.0]])]});}
            var Q2;
            {var subQ0=sQuery(id+"F0.wireOp",EDGE,"E183");Q2=makeQuery(id+"F0.imprint","IMPRINT",FACE,{"disambiguationData":[TD([[makeQuery(id+"F0.imprint","IMPRINT",EDGE,{"derivedFrom":subQ0}),1.0]])]});}
            var Q3;
            {var subQ0=sQuery(id+"F0.wireOp",EDGE,"E27");Q3=makeQuery(id+"F0.imprint","IMPRINT",FACE,{"disambiguationData":[TD([[makeQuery(id+"F0.imprint","IMPRINT",EDGE,{"derivedFrom":subQ0}),1.0]])]});}
            var Q4;
            {var subQ0=sQuery(id+"F0.wireOp",EDGE,"E30");Q4=makeQuery(id+"F0.imprint","IMPRINT",FACE,{"disambiguationData":[TD([[makeQuery(id+"F0.imprint","IMPRINT",EDGE,{"derivedFrom":subQ0}),1.0]])]});}
            var Q5;
            {var subQ0=sQuery(id+"F0.wireOp",EDGE,"E29");Q5=makeQuery(id+"F0.imprint","IMPRINT",FACE,{"disambiguationData":[TD([[makeQuery(id+"F0.imprint","IMPRINT",EDGE,{"derivedFrom":subQ0}),1.0]])]});}
            var Q6;
            {var subQ0=sQuery(id+"F0.wireOp",EDGE,"E48");Q6=makeQuery(id+"F0.imprint","IMPRINT",FACE,{"disambiguationData":[TD([[makeQuery(id+"F0.imprint","IMPRINT",EDGE,{"derivedFrom":subQ0}),1.0]])]});}
            var Q7;
            {var subQ0=sQuery(id+"F0.wireOp",EDGE,"E51");Q7=makeQuery(id+"F0.imprint","IMPRINT",FACE,{"disambiguationData":[TD([[makeQuery(id+"F0.imprint","IMPRINT",EDGE,{"derivedFrom":subQ0}),-1.0]])]});}
            var Q8;
            {var subQ0=sQuery(id+"F0.wireOp",EDGE,"E50");Q8=makeQuery(id+"F0.imprint","IMPRINT",FACE,{"disambiguationData":[TD([[makeQuery(id+"F0.imprint","IMPRINT",EDGE,{"derivedFrom":subQ0}),-1.0]])]});}
            extrude(context, id + "F10", {"entities" : qUnion([Q0, Q1, Q2, Q3, Q4, Q5, Q6, Q7, Q8]), "depth" : 3000 * mm, "offsetDistance" : 25 * mm});
        }
        {
            var Q0;
            Q0=makeQuery(id+"F5.opExtrude","CAP_FACE",FACE,{"disambiguationData":[OSD([sQuery(id+"F0.wireOp",EDGE,"E17"),sQuery(id+"F0.wireOp",EDGE,"E18"),sQuery(id+"F0.wireOp",EDGE,"E19"),sQuery(id+"F0.wireOp",EDGE,"E26"),sQuery(id+"F0.wireOp",EDGE,"E57"),sQuery(id+"F0.wireOp",EDGE,"E58"),sQuery(id+"F0.wireOp",EDGE,"E59"),sQuery(id+"F0.wireOp",EDGE,"E60"),sQuery(id+"F0.wireOp",EDGE,"E61"),sQuery(id+"F0.wireOp",EDGE,"E62"),sQuery(id+"F0.wireOp",EDGE,"E63"),sQuery(id+"F0.wireOp",EDGE,"E64"),sQuery(id+"F0.wireOp",EDGE,"E78"),sQuery(id+"F0.wireOp",EDGE,"E90"),sQuery(id+"F0.wireOp",EDGE,"E91"),sQuery(id+"F0.wireOp",EDGE,"E92"),sQuery(id+"F0.wireOp",EDGE,"E93"),sQuery(id+"F0.wireOp",EDGE,"E94"),sQuery(id+"F0.wireOp",EDGE,"E95"),sQuery(id+"F0.wireOp",EDGE,"E96"),sQuery(id+"F0.wireOp",EDGE,"E97"),sQuery(id+"F0.wireOp",EDGE,"E98"),sQuery(id+"F0.wireOp",EDGE,"E99"),sQuery(id+"F0.wireOp",EDGE,"E100"),sQuery(id+"F0.wireOp",EDGE,"E101"),sQuery(id+"F0.wireOp",EDGE,"E102"),sQuery(id+"F0.wireOp",EDGE,"E103"),sQuery(id+"F0.wireOp",EDGE,"E130"),sQuery(id+"F0.wireOp",EDGE,"E131"),sQuery(id+"F0.wireOp",EDGE,"E132"),sQuery(id+"F0.wireOp",EDGE,"E133"),sQuery(id+"F0.wireOp",EDGE,"E134"),sQuery(id+"F0.wireOp",EDGE,"E135"),sQuery(id+"F0.wireOp",EDGE,"E136"),sQuery(id+"F0.wireOp",EDGE,"E137"),sQuery(id+"F0.wireOp",EDGE,"E138"),sQuery(id+"F0.wireOp",EDGE,"E139"),sQuery(id+"F0.wireOp",EDGE,"E140"),sQuery(id+"F0.wireOp",EDGE,"E141"),sQuery(id+"F0.wireOp",EDGE,"E142"),sQuery(id+"F0.wireOp",EDGE,"E143"),sQuery(id+"F0.wireOp",EDGE,"E152"),sQuery(id+"F0.wireOp",EDGE,"E153"),sQuery(id+"F0.wireOp",EDGE,"E154"),sQuery(id+"F0.wireOp",EDGE,"E155"),sQuery(id+"F0.wireOp",EDGE,"E156"),sQuery(id+"F0.wireOp",EDGE,"E157"),sQuery(id+"F0.wireOp",EDGE,"E186"),sQuery(id+"F0.wireOp",EDGE,"E187"),sQuery(id+"F0.wireOp",EDGE,"E188"),sQuery(id+"F0.wireOp",EDGE,"E189"),sQuery(id+"F0.wireOp",EDGE,"E190"),sQuery(id+"F0.wireOp",EDGE,"E195"),sQuery(id+"F0.wireOp",EDGE,"E197"),sQuery(id+"F0.wireOp",EDGE,"E198"),sQuery(id+"F0.wireOp",EDGE,"E199"),sQuery(id+"F0.wireOp",EDGE,"E200"),sQuery(id+"F0.wireOp",EDGE,"E201"),sQuery(id+"F0.wireOp",EDGE,"E202")])],"isStart":true});
            var sketch = newSketch(context, id + "F11", { "sketchPlane" : qUnion([Q0])});
            skLineSegment(sketch, "E203.bottom", {"start": v(6209.41, 12233.27) * mm, "end": v(16036.02, 12233.27) * mm});
            skLineSegment(sketch, "E203.top", {"start": v(6209.41, 6200.83) * mm, "end": v(16036.02, 6200.83) * mm});
            skLineSegment(sketch, "E203.left", {"start": v(6209.41, 12233.27) * mm, "end": v(6209.41, 6200.83) * mm});
            skLineSegment(sketch, "E203.right", {"start": v(16036.02, 12233.27) * mm, "end": v(16036.02, 6200.83) * mm});
            skLineSegment(sketch, "E204.top", {"start": v(16036.02, 304.87) * mm, "end": v(12760.48, 304.87) * mm});
            skLineSegment(sketch, "E204.left", {"start": v(16036.02, 6200.83) * mm, "end": v(16036.02, 304.87) * mm});
            skLineSegment(sketch, "E204.right", {"start": v(12760.48, 12233.27) * mm, "end": v(12760.48, 304.87) * mm});
            skSolve(sketch);
        }
        {
            var Q0;
            Q0=makeQuery(id+"F10.opExtrude","SWEPT_FACE",FACE,{"disambiguationData":[OSD([sQuery(id+"F0.wireOp",EDGE,"E52")])]});
            var sketch = newSketch(context, id + "F12", { "sketchPlane" : qUnion([Q0])});
            skLineSegment(sketch, "E205.bottom", {"start": v(-9299.84, 2625.03) * mm, "end": v(-2299.84, 2625.03) * mm});
            skLineSegment(sketch, "E205.top", {"start": v(-9299.84, 2825.03) * mm, "end": v(-2299.84, 2825.03) * mm});
            skLineSegment(sketch, "E205.left", {"start": v(-9299.84, 2625.03) * mm, "end": v(-9299.84, 2825.03) * mm});
            skLineSegment(sketch, "E205.right", {"start": v(-2299.84, 2625.03) * mm, "end": v(-2299.84, 2825.03) * mm});
            skSolve(sketch);
        }
        {
            var Q0;
            Q0 = qSketchRegion(id + "F12", true);
            extrude(context, id + "F13", {"entities" : qUnion([Q0]), "depth" : 100 * mm, "offsetDistance" : 25 * mm});
        }
        {
            var Q0;
            {var subQ5=sQuery(id+"F11.wireOp",EDGE,"E203.left");Q0=makeQuery(id+"F11.imprint","IMPRINT",FACE,{"disambiguationData":[TD([[makeQuery(id+"F11.imprint","IMPRINT",EDGE,{"derivedFrom":subQ5}),-1.0]])]});}
            var sketch = newSketch(context, id + "F14", { "sketchPlane" : qUnion([Q0])});
            skCircle(sketch, "E206", {"center": v(11607.9, 3615.62) * mm, "radius": 253.15 * mm});
            skSolve(sketch);
        }
        {
            var Q0;
            Q0 = qSketchRegion(id + "F14", true);
            extrude(context, id + "F15", {"entities" : qUnion([Q0]), "depth" : 1800 * mm, "offsetDistance" : 25 * mm});
        }
    });
